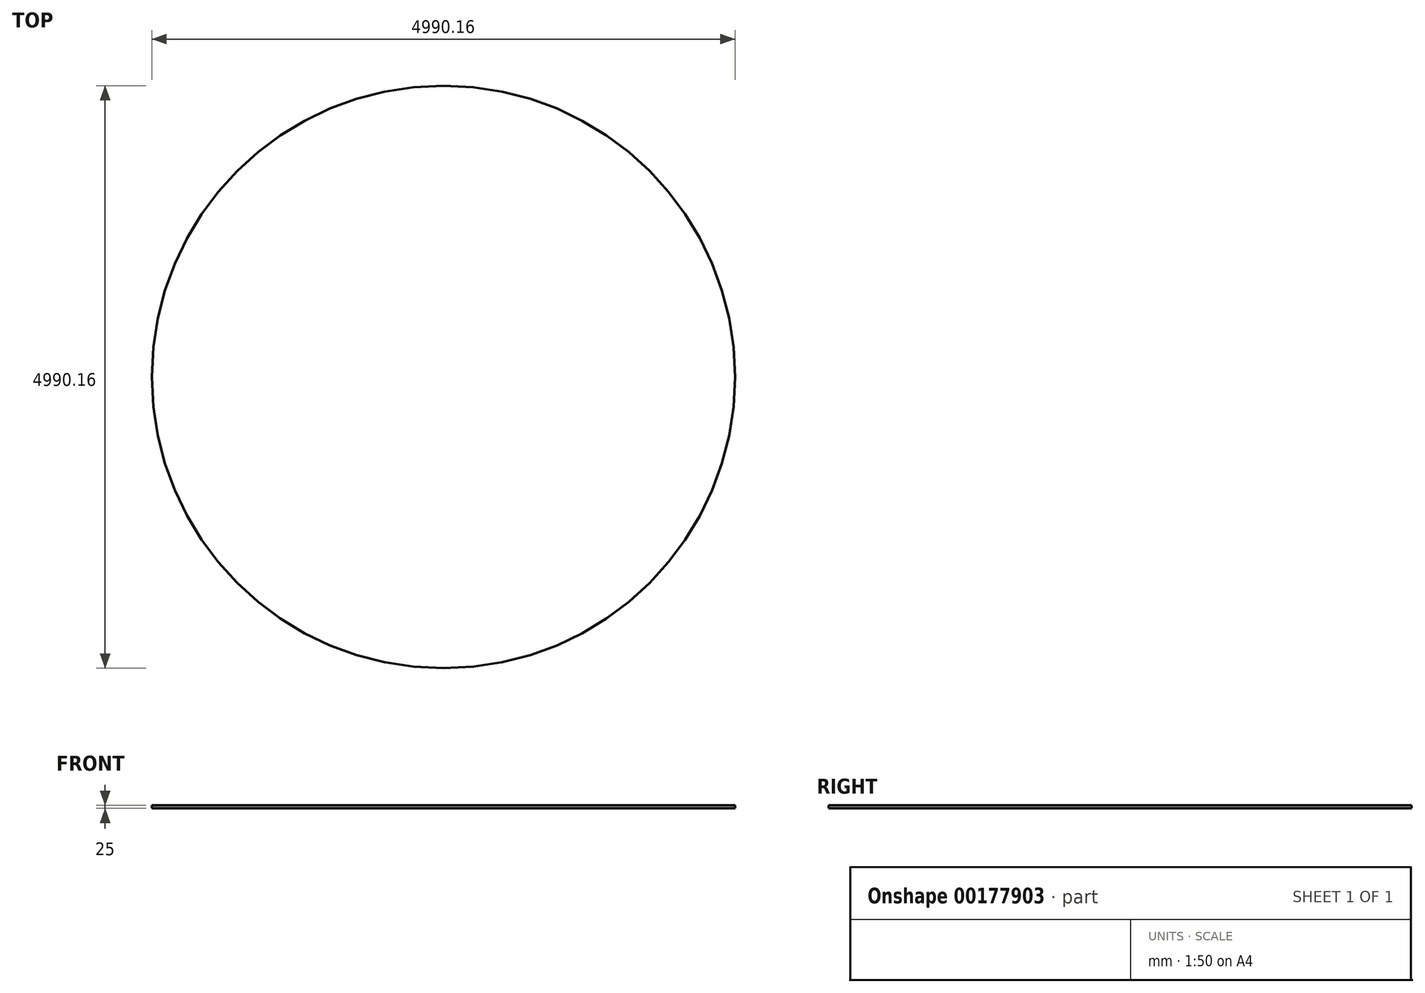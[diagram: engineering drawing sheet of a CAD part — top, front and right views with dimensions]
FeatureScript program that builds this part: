
annotation { "Feature Type Name" : "Feature", "Feature Type Description" : "" }
export const myFeature = defineFeature(function(context is Context, id is Id, definition is map)
    precondition{}
    {
        {
            var Q0;
            Q0=qCreatedBy(makeId("Top.planeOp"),FACE);
            var sketch = newSketch(context, id + "F0", { "sketchPlane" : qUnion([Q0])});
            skCircle(sketch, "E0", {"center": v(0, 0) * mm, "radius": 2495.08 * mm});
            skSolve(sketch);
        }
        {
            var Q0;
            Q0=sQuery(id+"F0.wireOp",EDGE,"DFzHkkZG-YlK9-2tXJ-gi90-Kk3Bbho5LjqZ");
            var Q1;
            Q1=sQuery(id+"F0.wireOp",EDGE,"E0");
            extrude(context, id + "F1", {"bodyType" : ToolBodyType.SURFACE, "surfaceEntities" : qUnion([Q0, Q1]), "depth" : 10000 * mm});
        }
        {
            var Q0;
            Q0 = qSketchRegion(id + "F0", true);
            extrude(context, id + "F2", {"entities" : qUnion([Q0]), "depth" : 25 * mm});
        }
    });
